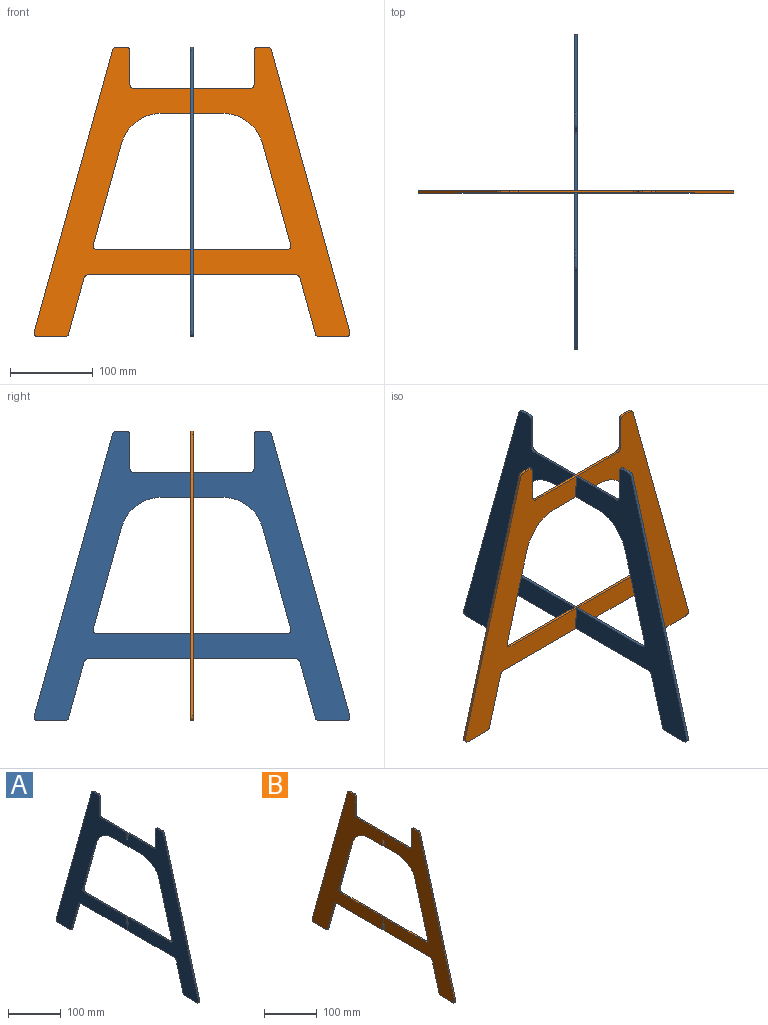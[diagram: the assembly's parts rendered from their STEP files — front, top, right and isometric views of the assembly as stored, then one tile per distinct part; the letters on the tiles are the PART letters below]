
ASSEMBLY  parts=2 mates=1
PART A: 46 faces, bbox 3x381.3x350 mm
  f0: plane 15x3mm, normal (0,-1,0), area 45mm2, adj f1,f29,f30,f31
  f1: plane 112.71x3mm, normal (0,0,1), area 338.1mm2, adj f0,f30,f31,f45
  f2: plane 122.04x33.9mm, normal (0,-0.96,-0.27), area 380mm2, adj f3,f30,f31,f45
  f3: cylinder r=50mm len=48.18mm, axis (1,0,0), area 195mm2, adj f2,f4,f30,f31
  f4: plane 73.99x3mm, normal (0,0,-1), area 222mm2, adj f3,f5,f30,f31
  f5: cylinder r=50mm len=48.18mm, axis (1,0,0), area 195mm2, adj f4,f6,f30,f31
  f6: plane 122.04x33.9mm, normal (0,0.96,-0.27), area 380mm2, adj f5,f30,f31,f42
  f7: plane 112.71x3mm, normal (0,0,1), area 338.1mm2, adj f8,f30,f31,f42
  f8: plane 15x3mm, normal (0,1,0), area 45mm2, adj f7,f9,f30,f31
  f9: plane 3x1.45mm, normal (0,0,1), area 4.3mm2, adj f8,f10,f30,f31
  f10: plane 15x3mm, normal (0,1,0), area 45mm2, adj f9,f11,f30,f31
  f11: plane 125.27x3mm, normal (0,0,-1), area 375.8mm2, adj f10,f30,f31,f44
  f12: plane 67.68x18.8mm, normal (0,0.96,-0.27), area 210.7mm2, adj f30,f31,f40,f44
  f13: plane 31.84x3mm, normal (0,0,-1), area 95.5mm2, adj f30,f31,f40,f41
  f14: plane 340x94.44mm, normal (0,-0.96,0.27), area 1058.6mm2, adj f30,f31,f41,f43
  f15: plane 11.2x3mm, normal (0,0,1), area 33.6mm2, adj f30,f31,f36,f43
  f16: plane 40x3mm, normal (0,1,0), area 120mm2, adj f30,f31,f36,f37
  f17: plane 68.45x3mm, normal (0,0,1), area 205.4mm2, adj f18,f30,f31,f37
  f18: plane 15x3mm, normal (0,1,0), area 45mm2, adj f17,f19,f30,f31
  f19: plane 3.1x3mm, normal (0,0,1), area 9.3mm2, adj f18,f20,f30,f31
  f20: plane 15x3mm, normal (0,-1,0), area 45mm2, adj f19,f21,f30,f31
  f21: plane 68.45x3mm, normal (0,0,1), area 205.4mm2, adj f20,f30,f31,f35
  f22: plane 40x3mm, normal (0,-1,0), area 120mm2, adj f30,f31,f34,f35
  f23: plane 11.2x3mm, normal (0,0,1), area 33.6mm2, adj f30,f31,f33,f34
  f24: plane 340x94.44mm, normal (0,0.96,0.27), area 1058.6mm2, adj f30,f31,f32,f33
  f25: plane 31.84x3mm, normal (0,0,-1), area 95.5mm2, adj f30,f31,f32,f38
  f26: plane 67.68x18.8mm, normal (0,-0.96,-0.27), area 210.7mm2, adj f30,f31,f38,f39
  f27: plane 125.27x3mm, normal (0,0,-1), area 375.8mm2, adj f28,f30,f31,f39
  f28: plane 15x3mm, normal (0,-1,0), area 45mm2, adj f27,f29,f30,f31
  f29: plane 3x1.45mm, normal (0,0,1), area 4.3mm2, adj f0,f28,f30,f31
  f30: plane 381.29x350mm, normal (-1,0,0), area 40227.1mm2, adj f0,f1,f2,f3,f4,f5,f6,f7
  f31: plane 381.29x350mm, normal (1,0,0), area 40227.1mm2, adj f0,f1,f2,f3,f4,f5,f6,f7
  f32: cylinder r=5mm len=6.34mm, axis (-1,0,0), area 27.6mm2, adj f24,f25,f30,f31
  f33: cylinder r=5mm len=4.82mm, axis (-1,0,0), area 19.5mm2, adj f23,f24,f30,f31
  f34: cylinder r=5mm len=5mm, axis (-1,0,0), area 23.6mm2, adj f22,f23,f30,f31
  f35: cylinder r=5mm len=5mm, axis (1,0,0), area 23.6mm2, adj f21,f22,f30,f31
  f36: cylinder r=5mm len=5mm, axis (-1,0,0), area 23.6mm2, adj f15,f16,f30,f31
  f37: cylinder r=5mm len=5mm, axis (1,0,0), area 23.6mm2, adj f16,f17,f30,f31
  f38: cylinder r=5mm len=4.82mm, axis (-1,0,0), area 19.5mm2, adj f25,f26,f30,f31
  f39: cylinder r=5mm len=4.82mm, axis (-1,0,0), area 19.5mm2, adj f26,f27,f30,f31
  f40: cylinder r=5mm len=4.82mm, axis (-1,0,0), area 19.5mm2, adj f12,f13,f30,f31
  f41: cylinder r=5mm len=6.34mm, axis (-1,0,0), area 27.6mm2, adj f13,f14,f30,f31
  f42: cylinder r=5mm len=6.34mm, axis (-1,0,0), area 27.6mm2, adj f6,f7,f30,f31
  f43: cylinder r=5mm len=4.82mm, axis (-1,0,0), area 19.5mm2, adj f14,f15,f30,f31
  f44: cylinder r=5mm len=4.82mm, axis (-1,0,0), area 19.5mm2, adj f11,f12,f30,f31
  f45: cylinder r=5mm len=6.34mm, axis (-1,0,0), area 27.6mm2, adj f1,f2,f30,f31
PART B: 46 faces, bbox 3x381.3x350 mm
  f0: plane 15x3mm, normal (0,-1,0), area 45mm2, adj f1,f29,f30,f31
  f1: plane 114.16x3mm, normal (0,0,1), area 342.5mm2, adj f0,f30,f31,f45
  f2: plane 122.04x33.9mm, normal (0,-0.96,-0.27), area 380mm2, adj f3,f30,f31,f45
  f3: cylinder r=50mm len=48.18mm, axis (1,0,0), area 195mm2, adj f2,f4,f30,f31
  f4: plane 35.45x3mm, normal (0,0,-1), area 106.3mm2, adj f3,f5,f30,f31
  f5: plane 15x3mm, normal (0,-1,0), area 45mm2, adj f4,f6,f30,f31
  f6: plane 3.1x3mm, normal (0,0,-1), area 9.3mm2, adj f5,f7,f30,f31
  f7: plane 15x3mm, normal (0,1,0), area 45mm2, adj f6,f8,f30,f31
  f8: plane 35.45x3mm, normal (0,0,-1), area 106.3mm2, adj f7,f9,f30,f31
  f9: cylinder r=50mm len=48.18mm, axis (1,0,0), area 195mm2, adj f8,f10,f30,f31
  f10: plane 122.04x33.9mm, normal (0,0.96,-0.27), area 380mm2, adj f9,f30,f31,f42
  f11: plane 114.16x3mm, normal (0,0,1), area 342.5mm2, adj f12,f30,f31,f42
  f12: plane 15x3mm, normal (0,1,0), area 45mm2, adj f11,f13,f30,f31
  f13: plane 3x1.45mm, normal (0,0,-1), area 4.3mm2, adj f12,f14,f30,f31
  f14: plane 15x3mm, normal (0,1,0), area 45mm2, adj f13,f15,f30,f31
  f15: plane 123.82x3mm, normal (0,0,-1), area 371.4mm2, adj f14,f30,f31,f44
  f16: plane 67.68x18.8mm, normal (0,0.96,-0.27), area 210.7mm2, adj f30,f31,f40,f44
  f17: plane 31.84x3mm, normal (0,0,-1), area 95.5mm2, adj f30,f31,f40,f41
  f18: plane 340x94.44mm, normal (0,-0.96,0.27), area 1058.6mm2, adj f30,f31,f41,f43
  f19: plane 11.2x3mm, normal (0,0,1), area 33.6mm2, adj f30,f31,f36,f43
  f20: plane 40x3mm, normal (0,1,0), area 120mm2, adj f30,f31,f36,f37
  f21: plane 140x3mm, normal (0,0,1), area 420mm2, adj f30,f31,f35,f37
  f22: plane 40x3mm, normal (0,-1,0), area 120mm2, adj f30,f31,f34,f35
  f23: plane 11.2x3mm, normal (0,0,1), area 33.6mm2, adj f30,f31,f33,f34
  f24: plane 340x94.44mm, normal (0,0.96,0.27), area 1058.6mm2, adj f30,f31,f32,f33
  f25: plane 31.84x3mm, normal (0,0,-1), area 95.5mm2, adj f30,f31,f32,f38
  f26: plane 67.68x18.8mm, normal (0,-0.96,-0.27), area 210.7mm2, adj f30,f31,f38,f39
  f27: plane 123.82x3mm, normal (0,0,-1), area 371.4mm2, adj f28,f30,f31,f39
  f28: plane 15x3mm, normal (0,-1,0), area 45mm2, adj f27,f29,f30,f31
  f29: plane 3x1.45mm, normal (0,0,-1), area 4.3mm2, adj f0,f28,f30,f31
  f30: plane 381.29x350mm, normal (-1,0,0), area 40227.1mm2, adj f0,f1,f2,f3,f4,f5,f6,f7
  f31: plane 381.29x350mm, normal (1,0,0), area 40227.1mm2, adj f0,f1,f2,f3,f4,f5,f6,f7
  f32: cylinder r=5mm len=6.34mm, axis (-1,0,0), area 27.6mm2, adj f24,f25,f30,f31
  f33: cylinder r=5mm len=4.82mm, axis (-1,0,0), area 19.5mm2, adj f23,f24,f30,f31
  f34: cylinder r=5mm len=5mm, axis (-1,0,0), area 23.6mm2, adj f22,f23,f30,f31
  f35: cylinder r=5mm len=5mm, axis (1,0,0), area 23.6mm2, adj f21,f22,f30,f31
  f36: cylinder r=5mm len=5mm, axis (-1,0,0), area 23.6mm2, adj f19,f20,f30,f31
  f37: cylinder r=5mm len=5mm, axis (1,0,0), area 23.6mm2, adj f20,f21,f30,f31
  f38: cylinder r=5mm len=4.82mm, axis (-1,0,0), area 19.5mm2, adj f25,f26,f30,f31
  f39: cylinder r=5mm len=4.82mm, axis (-1,0,0), area 19.5mm2, adj f26,f27,f30,f31
  f40: cylinder r=5mm len=4.82mm, axis (-1,0,0), area 19.5mm2, adj f16,f17,f30,f31
  f41: cylinder r=5mm len=6.34mm, axis (-1,0,0), area 27.6mm2, adj f17,f18,f30,f31
  f42: cylinder r=5mm len=6.34mm, axis (-1,0,0), area 27.6mm2, adj f10,f11,f30,f31
  f43: cylinder r=5mm len=4.82mm, axis (-1,0,0), area 19.5mm2, adj f18,f19,f30,f31
  f44: cylinder r=5mm len=4.82mm, axis (-1,0,0), area 19.5mm2, adj f15,f16,f30,f31
  f45: cylinder r=5mm len=6.34mm, axis (-1,0,0), area 27.6mm2, adj f1,f2,f30,f31
PLACE A at identity fixed
PLACE B rot(axis=(0,0,-1),90deg) t=(1.5,1.5,0)mm
MATE planar A.f19 <-> B.f6  axis (0,0,1) through (1.5,0,150)mm
